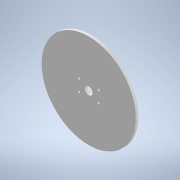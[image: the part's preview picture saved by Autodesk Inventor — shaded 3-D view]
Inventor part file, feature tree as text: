
AUTODESK INVENTOR PART (.ipt)
format: ipt  version: 2021 (Build 250183000, 183)  size: 105,472 bytes
history: native  units: mm
features: sketch x4, hole x2, other x1, extrude x1
ambient origin geometry x8: Origin, YZ Plane, XZ Plane, XY Plane, X Axis, Y Axis, Z Axis, Center Point
bodies: Body1 (feature_tree)
feature tree (8):
  other  "Sólido1"
  extrude  "Extrusión1"  [1 undecoded]
  hole  "Agujero1"  [1 undecoded]
  hole  "Agujero2"  [1 undecoded]
  sketch  "Boceto4"
  sketch  "Boceto1"  dims[d1=3.0mm d2=0.0mm]
  sketch  "Boceto2"  dims[d4=9.0mm d5=6.0mm d6=4.0mm d7=2.0mm d8=90.0deg d9=8.0mm d10=20.594885mm]
  sketch  "Boceto3"  dims[d20=2.5mm d21=6.0mm d22=4.0mm d23=2.0mm d24=90.0deg d25=8.0mm d26=20.594885mm]
note: 3 required parameter values undecoded (feature->parameter linkage not recoverable at this tier; creation-order binding heuristic only, values carry confidence <= 0.55)
